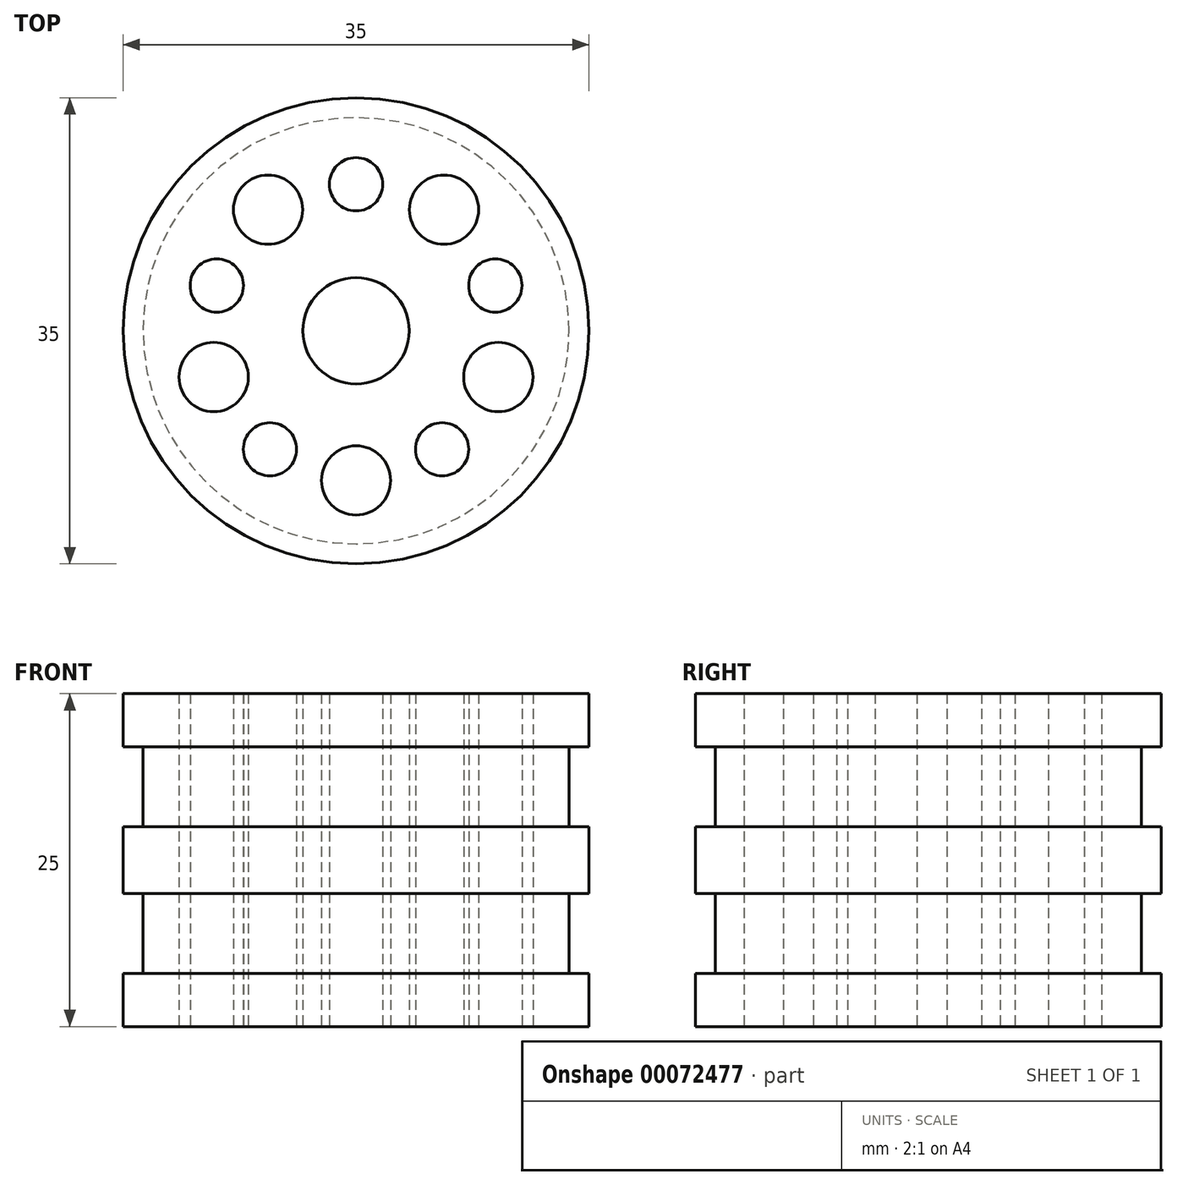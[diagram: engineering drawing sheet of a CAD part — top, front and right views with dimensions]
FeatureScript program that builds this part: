
annotation { "Feature Type Name" : "Feature", "Feature Type Description" : "" }
export const myFeature = defineFeature(function(context is Context, id is Id, definition is map)
    precondition{}
    {
        {
            var Q0;
            Q0=qCreatedBy(makeId("Top.planeOp"),FACE);
            var sketch = newSketch(context, id + "F0", { "sketchPlane" : qUnion([Q0])});
            skCircle(sketch, "E0", {"center": v(0, 0) * mm, "radius": 17.5 * mm});
            skCircle(sketch, "E1", {"center": v(0, 0) * mm, "radius": 15.95 * mm});
            skLineSegment(sketch, "E2", {"start": v(0, 0) * mm, "end": v(0, 11) * mm, "construction": true});
            skCircle(sketch, "E3", {"center": v(0, 11) * mm, "radius": 2 * mm});
            skCircle(sketch, "E4.1.0", {"center": v(-10.46, 3.4) * mm, "radius": 2 * mm});
            skCircle(sketch, "E4.2.0", {"center": v(-6.47, -8.9) * mm, "radius": 2 * mm});
            skCircle(sketch, "E4.3.0", {"center": v(6.47, -8.9) * mm, "radius": 2 * mm});
            skCircle(sketch, "E4.4.0", {"center": v(10.46, 3.4) * mm, "radius": 2 * mm});
            skCircle(sketch, "E5", {"center": v(0, 0) * mm, "radius": 4 * mm});
            skLineSegment(sketch, "E6", {"start": v(-10.46, 3.4) * mm, "end": v(0, 11) * mm, "construction": true});
            skLineSegment(sketch, "E7", {"start": v(0, 0) * mm, "end": v(-6.6, 9.1) * mm, "construction": true});
            skCircle(sketch, "E8", {"center": v(-6.6, 9.1) * mm, "radius": 2.6 * mm});
            skCircle(sketch, "E9.1.0", {"center": v(-10.69, -3.47) * mm, "radius": 2.6 * mm});
            skCircle(sketch, "E9.2.0", {"center": v(0, -11.24) * mm, "radius": 2.6 * mm});
            skCircle(sketch, "E9.3.0", {"center": v(10.69, -3.47) * mm, "radius": 2.6 * mm});
            skCircle(sketch, "E9.4.0", {"center": v(6.6, 9.1) * mm, "radius": 2.6 * mm});
            skSolve(sketch);
        }
        {
            var Q0;
            Q0=makeQuery(id+"F0.imprint","IMPRINT",FACE,{"disambiguationData":[TD([[makeQuery(id+"F0.imprint","IMPRINT",EDGE,{"derivedFrom":sQuery(id+"F0.wireOp",EDGE,"E0")}),1.0]])]});
            var Q1;
            Q1=makeQuery(id+"F0.imprint","IMPRINT",FACE,{"disambiguationData":[TD([[makeQuery(id+"F0.imprint","IMPRINT",EDGE,{"derivedFrom":sQuery(id+"F0.wireOp",EDGE,"E1")}),1.0]])]});
            extrude(context, id + "F1", {"entities" : qUnion([Q0, Q1]), "depth" : 25 * mm, "symmetric" : true});
        }
        {
            var Q0;
            Q0=makeQuery(id+"F1.opExtrude","CAP_FACE",FACE,{"disambiguationData":[OSD([sQuery(id+"F0.wireOp",EDGE,"E0"),sQuery(id+"F0.wireOp",EDGE,"E3"),sQuery(id+"F0.wireOp",EDGE,"E4.1.0"),sQuery(id+"F0.wireOp",EDGE,"E4.2.0"),sQuery(id+"F0.wireOp",EDGE,"E4.3.0"),sQuery(id+"F0.wireOp",EDGE,"E4.4.0"),sQuery(id+"F0.wireOp",EDGE,"E5"),sQuery(id+"F0.wireOp",EDGE,"E8"),sQuery(id+"F0.wireOp",EDGE,"E9.1.0"),sQuery(id+"F0.wireOp",EDGE,"E9.2.0"),sQuery(id+"F0.wireOp",EDGE,"E9.3.0"),sQuery(id+"F0.wireOp",EDGE,"E9.4.0")])],"isStart":false});
            var sketch = newSketch(context, id + "F2", { "sketchPlane" : qUnion([Q0])});
            skCircle(sketch, "E10", {"center": v(0, 0) * mm, "radius": 16 * mm});
            skSolve(sketch);
        }
        {
            var Q0;
            Q0=makeQuery(id+"F2.imprint","IMPRINT",FACE,{"disambiguationData":[TD([[makeQuery(id+"F2.imprint","IMPRINT",EDGE,{"derivedFrom":sQuery(id+"F2.wireOp",EDGE,"E10")}),-1.0]])]});
            extrude(context, id + "F3", {"entities" : qUnion([Q0]), "operationType" : NewBodyOperationType.REMOVE, "oppositeDirection" : true, "depth" : 10 * mm, "hasSecondDirection" : true, "secondDirectionOppositeDirection" : true, "secondDirectionDepth" : 4 * mm});
        }
        {
            var Q0;
            Q0=makeQuery(id+"F1.opExtrude","CAP_FACE",FACE,{"disambiguationData":[OSD([sQuery(id+"F0.wireOp",EDGE,"E0"),sQuery(id+"F0.wireOp",EDGE,"E3"),sQuery(id+"F0.wireOp",EDGE,"E4.1.0"),sQuery(id+"F0.wireOp",EDGE,"E4.2.0"),sQuery(id+"F0.wireOp",EDGE,"E4.3.0"),sQuery(id+"F0.wireOp",EDGE,"E4.4.0"),sQuery(id+"F0.wireOp",EDGE,"E5"),sQuery(id+"F0.wireOp",EDGE,"E8"),sQuery(id+"F0.wireOp",EDGE,"E9.1.0"),sQuery(id+"F0.wireOp",EDGE,"E9.2.0"),sQuery(id+"F0.wireOp",EDGE,"E9.3.0"),sQuery(id+"F0.wireOp",EDGE,"E9.4.0")])],"isStart":true});
            var sketch = newSketch(context, id + "F4", { "sketchPlane" : qUnion([Q0])});
            skCircle(sketch, "E11", {"center": v(0, 0) * mm, "radius": 16 * mm});
            skSolve(sketch);
        }
        {
            var Q0;
            Q0=makeQuery(id+"F4.imprint","IMPRINT",FACE,{"disambiguationData":[TD([[makeQuery(id+"F4.imprint","IMPRINT",EDGE,{"derivedFrom":sQuery(id+"F4.wireOp",EDGE,"E11")}),-1.0]])]});
            extrude(context, id + "F5", {"entities" : qUnion([Q0]), "operationType" : NewBodyOperationType.REMOVE, "oppositeDirection" : true, "depth" : 10 * mm, "hasSecondDirection" : true, "secondDirectionOppositeDirection" : true, "secondDirectionDepth" : 4 * mm});
        }
    });
